# Revit family: 63_UN_Spot_Polar 10W D105_Natec
name_source: partatom
category: Lighting Fixtures
units: mm (PartAtom-declared; Revit-internal decimal feet)

## family parameters
Always vertical = Yes
Cut with Voids When Loaded = Yes
Light Source = Yes
OmniClass Number = 23.80.70.11.14.11
OmniClass Title = Downlights
Part Type = Normal
Room Calculation Point = Yes
Round Connector Dimension = Use Diameter
Shared = No
Work Plane-Based = No

## types (2) — shared parameters
Apparent Load = 10 VA
Assembly Code = 63.0
Color Filter = 16777215
Dimming Lamp Color Temperature Shift = <None>
Housing_Material = Laminate, White
IfcExportAs = IfcLightFixtureType
IfcExportType = USERDEFINED
Lamp = LED
Luminous Flux (lm) = 860 lm
Manufacturer = Natec Lighting
Model = Spot
Tilt Angle = 90.00°
Type Comments = Polar 6W D81
URL = https://nateclighting.nl
Voltage = 230 V
Wattage Comments = 10W

## per-type parameters (varying)
| type | Photometric Web File |
| Polar 10W 3000K | Polar 10W 3000K.IES |
| Polar 10W 4000K | Polar 10W 4000K.IES |

## geometry (parser evidence)
native form markers: Sweep x6
no freeform markers — native parametric forms only
